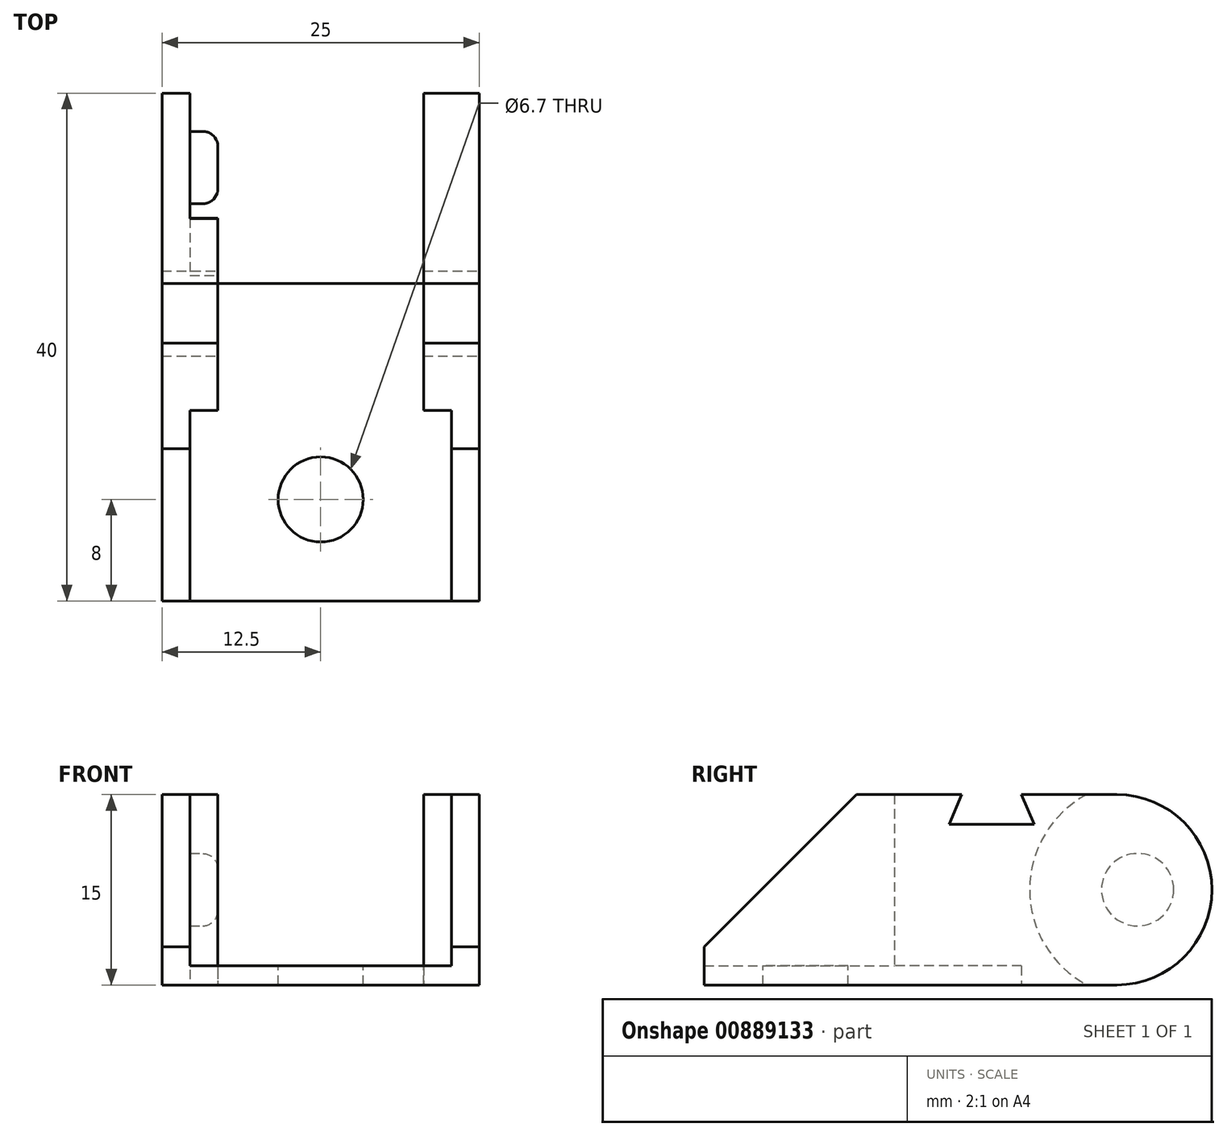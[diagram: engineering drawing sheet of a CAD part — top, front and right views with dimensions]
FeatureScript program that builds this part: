
annotation { "Feature Type Name" : "Feature", "Feature Type Description" : "" }
export const myFeature = defineFeature(function(context is Context, id is Id, definition is map)
    precondition{}
    {
        {
            var Q0;
            Q0=qCreatedBy(makeId("Top.planeOp"),FACE);
            var sketch = newSketch(context, id + "F0", { "sketchPlane" : qUnion([Q0])});
            skLineSegment(sketch, "E0.bottom", {"start": v(12.5, 20) * mm, "end": v(-12.5, 20) * mm});
            skLineSegment(sketch, "E0.top", {"start": v(12.5, -20) * mm, "end": v(-12.5, -20) * mm});
            skLineSegment(sketch, "E0.left", {"start": v(12.5, 20) * mm, "end": v(12.5, -20) * mm});
            skLineSegment(sketch, "E0.right", {"start": v(-12.5, 20) * mm, "end": v(-12.5, -20) * mm});
            skPoint(sketch, "E0.middle", {"position": v(0, 0) * mm});
            skLineSegment(sketch, "E1.bottom", {"start": v(-12.5, 20) * mm, "end": v(-8.1, 20) * mm});
            skLineSegment(sketch, "E1.top", {"start": v(-12.5, -20) * mm, "end": v(-8.1, -20) * mm});
            skLineSegment(sketch, "E1.right", {"start": v(-8.1, 20) * mm, "end": v(-8.1, -20) * mm});
            skLineSegment(sketch, "E2.bottom", {"start": v(12.5, 20) * mm, "end": v(8.1, 20) * mm});
            skLineSegment(sketch, "E2.top", {"start": v(12.5, -20) * mm, "end": v(8.1, -20) * mm});
            skLineSegment(sketch, "E2.right", {"start": v(8.1, 20) * mm, "end": v(8.1, -20) * mm});
            skLineSegment(sketch, "E3", {"start": v(-12.5, 5) * mm, "end": v(-8.1, 5) * mm});
            skLineSegment(sketch, "E4", {"start": v(-8.1, 5) * mm, "end": v(-8.1, 0.4) * mm});
            skLineSegment(sketch, "E5", {"start": v(-8.1, 0.4) * mm, "end": v(-12.5, 0.4) * mm});
            skLineSegment(sketch, "E6.MirrorCS", {"start": v(8.1, 0.4) * mm, "end": v(12.5, 0.4) * mm});
            skLineSegment(sketch, "E7.MirrorCS", {"start": v(12.5, 5) * mm, "end": v(8.1, 5) * mm});
            skLineSegment(sketch, "E8.bottom", {"start": v(-8.1, 20) * mm, "end": v(8.1, 20) * mm});
            skLineSegment(sketch, "E8.top", {"start": v(-8.1, 5) * mm, "end": v(8.1, 5) * mm});
            skLineSegment(sketch, "E8.left", {"start": v(-8.1, 20) * mm, "end": v(-8.1, 5) * mm});
            skLineSegment(sketch, "E8.right", {"start": v(8.1, 20) * mm, "end": v(8.1, 5) * mm});
            skLineSegment(sketch, "E9.bottom", {"start": v(-12.5, -20) * mm, "end": v(-10.3, -20) * mm});
            skLineSegment(sketch, "E9.top", {"start": v(-12.5, -5) * mm, "end": v(-10.3, -5) * mm});
            skLineSegment(sketch, "E9.left", {"start": v(-12.5, -20) * mm, "end": v(-12.5, -5) * mm});
            skLineSegment(sketch, "E9.right", {"start": v(-10.3, -20) * mm, "end": v(-10.3, -5) * mm});
            skLineSegment(sketch, "E10.bottom", {"start": v(12.5, -20) * mm, "end": v(10.3, -20) * mm});
            skLineSegment(sketch, "E10.top", {"start": v(12.5, -5) * mm, "end": v(10.3, -5) * mm});
            skLineSegment(sketch, "E10.left", {"start": v(12.5, -20) * mm, "end": v(12.5, -5) * mm});
            skLineSegment(sketch, "E10.right", {"start": v(10.3, -20) * mm, "end": v(10.3, -5) * mm});
            skLineSegment(sketch, "E11", {"start": v(-10.3, -5) * mm, "end": v(-8.1, -5) * mm});
            skLineSegment(sketch, "E12", {"start": v(10.3, -5) * mm, "end": v(8.1, -5) * mm});
            skSolve(sketch);
        }
        {
            var Q0;
            {var subQ2=sQuery(id+"F0.wireOp",EDGE,"E8.top");Q0=makeQuery(id+"F0.imprint","IMPRINT",FACE,{"disambiguationData":[TD([[makeQuery(id+"F0.imprint","IMPRINT",EDGE,{"derivedFrom":subQ2}),-1.0]])]});}
            var Q1;
            {var subQ0=sQuery(id+"F0.wireOp",EDGE,"E9.right");Q1=makeQuery(id+"F0.imprint","IMPRINT",FACE,{"disambiguationData":[TD([[makeQuery(id+"F0.imprint","IMPRINT",EDGE,{"derivedFrom":subQ0}),-1.0]])]});}
            var Q2;
            {var subQ3=sQuery(id+"F0.wireOp",EDGE,"E10.right");Q2=makeQuery(id+"F0.imprint","IMPRINT",FACE,{"disambiguationData":[TD([[makeQuery(id+"F0.imprint","IMPRINT",EDGE,{"derivedFrom":subQ3}),1.0]])]});}
            extrude(context, id + "F1", {"entities" : qUnion([Q0, Q1, Q2]), "depth" : 1.5 * mm, "offsetDistance" : 25 * mm});
        }
        {
            var Q0;
            {var subQ5=sQuery(id+"F0.wireOp",EDGE,"E3");Q0=makeQuery(id+"F0.imprint","IMPRINT",FACE,{"disambiguationData":[TD([[makeQuery(id+"F0.imprint","IMPRINT",EDGE,{"derivedFrom":subQ5}),1.0]])]});}
            var Q1;
            {var subQ5=sQuery(id+"F0.wireOp",EDGE,"E7.MirrorCS");Q1=makeQuery(id+"F0.imprint","IMPRINT",FACE,{"disambiguationData":[TD([[makeQuery(id+"F0.imprint","IMPRINT",EDGE,{"derivedFrom":subQ5}),-1.0]])]});}
            var Q2;
            {var subQ2=sQuery(id+"F0.wireOp",EDGE,"E3");Q2=makeQuery(id+"F0.imprint","IMPRINT",FACE,{"disambiguationData":[TD([[makeQuery(id+"F0.imprint","IMPRINT",EDGE,{"derivedFrom":subQ2}),-1.0]])]});}
            var Q3;
            {var subQ0=sQuery(id+"F0.wireOp",EDGE,"E6.MirrorCS");Q3=makeQuery(id+"F0.imprint","IMPRINT",FACE,{"disambiguationData":[TD([[makeQuery(id+"F0.imprint","IMPRINT",EDGE,{"derivedFrom":subQ0}),1.0]])]});}
            var Q4;
            {var subQ4=sQuery(id+"F0.wireOp",EDGE,"E9.top");Q4=makeQuery(id+"F0.imprint","IMPRINT",FACE,{"disambiguationData":[TD([[makeQuery(id+"F0.imprint","IMPRINT",EDGE,{"derivedFrom":subQ4}),-1.0]])]});}
            var Q5;
            {var subQ0=sQuery(id+"F0.wireOp",EDGE,"E5");Q5=makeQuery(id+"F0.imprint","IMPRINT",FACE,{"disambiguationData":[TD([[makeQuery(id+"F0.imprint","IMPRINT",EDGE,{"derivedFrom":subQ0}),1.0]])]});}
            var Q6;
            {var subQ1=sQuery(id+"F0.wireOp",EDGE,"E6.MirrorCS");Q6=makeQuery(id+"F0.imprint","IMPRINT",FACE,{"disambiguationData":[TD([[makeQuery(id+"F0.imprint","IMPRINT",EDGE,{"derivedFrom":subQ1}),-1.0]])]});}
            var Q7;
            {var subQ4=sQuery(id+"F0.wireOp",EDGE,"E10.top");Q7=makeQuery(id+"F0.imprint","IMPRINT",FACE,{"disambiguationData":[TD([[makeQuery(id+"F0.imprint","IMPRINT",EDGE,{"derivedFrom":subQ4}),1.0]])]});}
            extrude(context, id + "F2", {"entities" : qUnion([Q0, Q1, Q2, Q3, Q4, Q5, Q6, Q7]), "operationType" : NewBodyOperationType.ADD, "depth" : 15 * mm, "offsetDistance" : 25 * mm});
        }
        {
            var Q0;
            {var subQ0=sQuery(id+"F0.wireOp",EDGE,"E0.top");Q0=makeQuery(id+"F2.opExtrude","CAP_EDGE",EDGE,{"disambiguationData":[OSD([subQ0]),TDD([makeQuery(id+"F0.imprint","IMPRINT",EDGE,{"disambiguationData":[TD([[makeQuery(id+"F0.imprint","INTERSECT",VERTEX,{"derivedFrom":[subQ0,sQuery(id+"F0.wireOp",EDGE,"E10.right")]}),1.0]])],"derivedFrom":subQ0})])],"isStart":false});}
            var Q1;
            {var subQ0=sQuery(id+"F0.wireOp",EDGE,"E0.top");Q1=makeQuery(id+"F2.opExtrude","CAP_EDGE",EDGE,{"disambiguationData":[OSD([subQ0]),TDD([makeQuery(id+"F0.imprint","IMPRINT",EDGE,{"disambiguationData":[TD([[makeQuery(id+"F0.imprint","INTERSECT",VERTEX,{"derivedFrom":[subQ0,sQuery(id+"F0.wireOp",EDGE,"E0.right")]}),1.0]])],"derivedFrom":subQ0})])],"isStart":false});}
            chamfer(context, id + "F3", {"entities" : qUnion([Q0, Q1]), "width" : 12 * mm, "tangentPropagation" : true});
        }
        {
            var Q0;
            Q0=makeQuery(id+"F2.opExtrude","SWEPT_FACE",FACE,{"disambiguationData":[OSD([sQuery(id+"F0.wireOp",EDGE,"E0.left")])]});
            var sketch = newSketch(context, id + "F4", { "sketchPlane" : qUnion([Q0])});
            skLineSegment(sketch, "E13", {"start": v(5, 15) * mm, "end": v(6, 12.65) * mm});
            skLineSegment(sketch, "E14", {"start": v(6, 12.65) * mm, "end": v(-0.7, 12.65) * mm});
            skLineSegment(sketch, "E15", {"start": v(-0.7, 12.65) * mm, "end": v(0.3, 15) * mm});
            skSolve(sketch);
        }
        {
            var Q0;
            {var subQ0=sQuery(id+"F4.wireOp",EDGE,"E13");Q0=makeQuery(id+"F4.imprint","IMPRINT",FACE,{"disambiguationData":[TD([[makeQuery(id+"F4.imprint","IMPRINT",EDGE,{"derivedFrom":subQ0}),-1.0]])]});}
            extrude(context, id + "F5", {"entities" : qUnion([Q0]), "operationType" : NewBodyOperationType.REMOVE, "oppositeDirection" : true, "depth" : 25 * mm, "offsetDistance" : 25 * mm});
        }
        {
            var Q0;
            Q0=makeQuery(id+"F2.opExtrude","SWEPT_FACE",FACE,{"disambiguationData":[OSD([sQuery(id+"F0.wireOp",EDGE,"E1.right")])]});
            var sketch = newSketch(context, id + "F6", { "sketchPlane" : qUnion([Q0])});
            skCircle(sketch, "E16", {"center": v(14.15, 7.5) * mm, "radius": 2.85 * mm});
            skCircle(sketch, "E17", {"center": v(14.15, 7.5) * mm, "radius": 8.5 * mm});
            skSolve(sketch);
        }
        {
            var Q0;
            Q0=makeQuery(id+"F6.imprint","IMPRINT",FACE,{"disambiguationData":[TD([[makeQuery(id+"F6.imprint","IMPRINT",EDGE,{"derivedFrom":sQuery(id+"F6.wireOp",EDGE,"E16")}),-1.0]])]});
            extrude(context, id + "F7", {"entities" : qUnion([Q0]), "operationType" : NewBodyOperationType.REMOVE, "oppositeDirection" : true, "depth" : 2.2 * mm, "offsetDistance" : 25 * mm});
        }
        {
            var Q0;
            Q0=makeQuery(id+"F7.boolean.opBoolean","COPY",EDGE,{"derivedFrom":makeQuery(id+"F7.opExtrude","CAP_EDGE",EDGE,{"disambiguationData":[OSD([sQuery(id+"F6.wireOp",EDGE,"E16")])],"isStart":true})});
            fillet(context, id + "F8", {"entities" : qUnion([Q0]), "radius" : 1.2 * mm, "tangentPropagation" : true, "allowEdgeOverflow" : false});
        }
        {
            var Q0;
            {var subQ0=sQuery(id+"F0.wireOp",EDGE,"E0.bottom");Q0=makeQuery(id+"F2.opExtrude","CAP_EDGE",EDGE,{"disambiguationData":[OSD([subQ0]),TDD([makeQuery(id+"F0.imprint","IMPRINT",EDGE,{"disambiguationData":[TD([[makeQuery(id+"F0.imprint","INTERSECT",VERTEX,{"derivedFrom":[subQ0,sQuery(id+"F0.wireOp",EDGE,"E0.right")]}),1.0]])],"derivedFrom":subQ0})])],"isStart":false});}
            var Q1;
            {var subQ0=sQuery(id+"F0.wireOp",EDGE,"E0.bottom");Q1=makeQuery(id+"F2.opExtrude","CAP_EDGE",EDGE,{"disambiguationData":[OSD([subQ0]),TDD([makeQuery(id+"F0.imprint","IMPRINT",EDGE,{"disambiguationData":[TD([[makeQuery(id+"F0.imprint","INTERSECT",VERTEX,{"derivedFrom":[subQ0,sQuery(id+"F0.wireOp",EDGE,"E0.right")]}),1.0]])],"derivedFrom":subQ0})])],"isStart":true});}
            var Q2;
            {var subQ0=sQuery(id+"F0.wireOp",EDGE,"E0.bottom");Q2=makeQuery(id+"F2.opExtrude","CAP_EDGE",EDGE,{"disambiguationData":[OSD([subQ0]),TDD([makeQuery(id+"F0.imprint","IMPRINT",EDGE,{"disambiguationData":[TD([[makeQuery(id+"F0.imprint","INTERSECT",VERTEX,{"derivedFrom":[subQ0,sQuery(id+"F0.wireOp",EDGE,"E2.right")]}),1.0]])],"derivedFrom":subQ0})])],"isStart":false});}
            var Q3;
            {var subQ0=sQuery(id+"F0.wireOp",EDGE,"E0.bottom");Q3=makeQuery(id+"F2.opExtrude","CAP_EDGE",EDGE,{"disambiguationData":[OSD([subQ0]),TDD([makeQuery(id+"F0.imprint","IMPRINT",EDGE,{"disambiguationData":[TD([[makeQuery(id+"F0.imprint","INTERSECT",VERTEX,{"derivedFrom":[subQ0,sQuery(id+"F0.wireOp",EDGE,"E2.right")]}),1.0]])],"derivedFrom":subQ0})])],"isStart":true});}
            fillet(context, id + "F9", {"entities" : qUnion([Q0, Q1, Q2, Q3]), "radius" : 7.5 * mm, "tangentPropagation" : true, "allowEdgeOverflow" : false});
        }
        {
            var Q0;
            Q0=makeQuery(id+"F1.opExtrude","CAP_FACE",FACE,{"disambiguationData":[OSD([sQuery(id+"F0.wireOp",EDGE,"E0.top"),sQuery(id+"F0.wireOp",EDGE,"E1.right"),sQuery(id+"F0.wireOp",EDGE,"E2.right"),sQuery(id+"F0.wireOp",EDGE,"E8.top"),sQuery(id+"F0.wireOp",EDGE,"E9.right"),sQuery(id+"F0.wireOp",EDGE,"E10.right"),sQuery(id+"F0.wireOp",EDGE,"E11"),sQuery(id+"F0.wireOp",EDGE,"E12")])],"isStart":false});
            var sketch = newSketch(context, id + "F10", { "sketchPlane" : qUnion([Q0])});
            skCircle(sketch, "E18", {"center": v(0, -12) * mm, "radius": 3.35 * mm});
            skSolve(sketch);
        }
        {
            var Q0;
            Q0=makeQuery(id+"F10.imprint","IMPRINT",FACE,{"disambiguationData":[TD([[makeQuery(id+"F10.imprint","IMPRINT",EDGE,{"derivedFrom":sQuery(id+"F10.wireOp",EDGE,"E18")}),1.0]])]});
            extrude(context, id + "F11", {"entities" : qUnion([Q0]), "operationType" : NewBodyOperationType.REMOVE, "oppositeDirection" : true, "depth" : 25 * mm, "offsetDistance" : 25 * mm});
        }
    });
